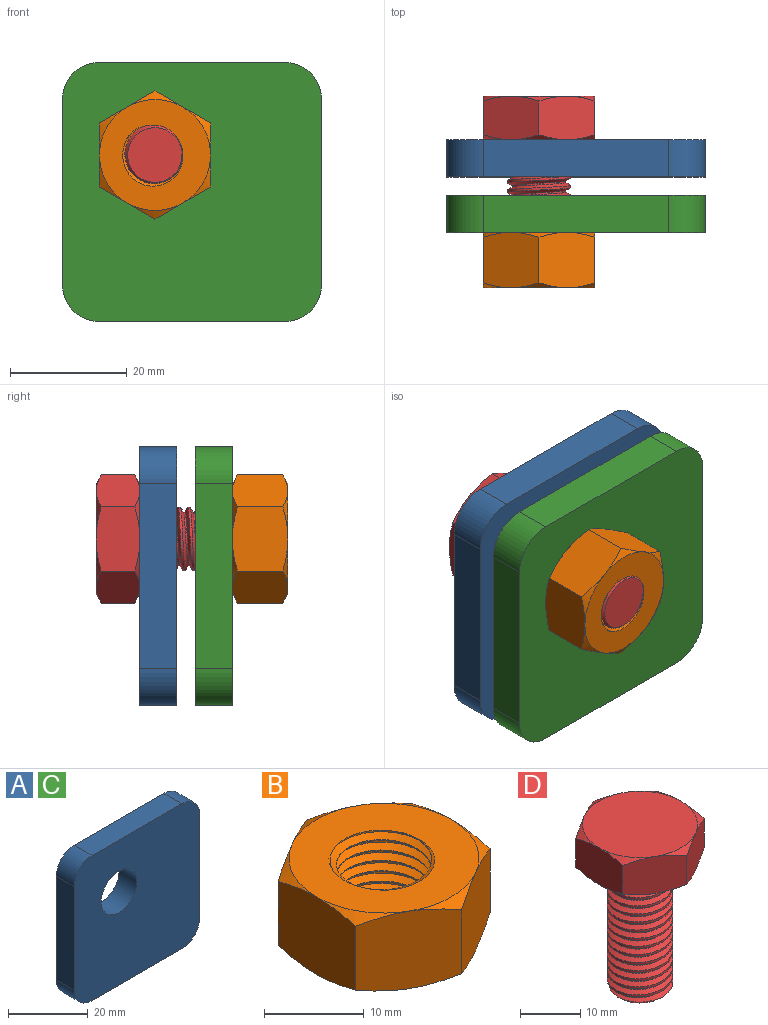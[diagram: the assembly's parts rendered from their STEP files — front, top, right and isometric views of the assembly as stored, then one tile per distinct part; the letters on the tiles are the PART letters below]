
ASSEMBLY  parts=4 mates=3
PART A: 11 faces, bbox 44.5x6.4x44.5 mm
  f0: plane 31.75x6.35mm, normal (0,0,-1), area 201.6mm2, adj f5,f6,f7,f10
  f1: plane 31.75x6.35mm, normal (1,0,0), area 201.6mm2, adj f5,f6,f7,f8
  f2: plane 31.75x6.35mm, normal (0,0,1), area 201.6mm2, adj f5,f6,f8,f9
  f3: cylinder r=6.35mm len=12.7mm, axis (0,1,0), area 253.4mm2, adj f5,f6
  f4: plane 31.75x6.35mm, normal (-1,0,0), area 201.6mm2, adj f5,f6,f9,f10
  f5: plane 44.45x44.45mm, normal (0,-1,0), area 1814.5mm2, adj f0,f1,f2,f3,f4,f7,f8,f9
  f6: plane 44.45x44.45mm, normal (0,1,0), area 1814.5mm2, adj f0,f1,f2,f3,f4,f7,f8,f9
  f7: cylinder r=6.35mm len=6.35mm, axis (0,1,0), area 63.3mm2, adj f0,f1,f5,f6
  f8: cylinder r=6.35mm len=6.35mm, axis (0,1,0), area 63.3mm2, adj f1,f2,f5,f6
  f9: cylinder r=6.35mm len=6.35mm, axis (0,1,0), area 63.3mm2, adj f2,f4,f5,f6
  f10: cylinder r=6.35mm len=6.35mm, axis (0,1,0), area 63.3mm2, adj f0,f4,f5,f6
PART B: 25 faces, bbox 22.9x22.9x11 mm
  f0: plane 19.49x19.49mm, normal (0,0,1), area 199.5mm2, adj f2,f5,f6,f8,f10,f12,f14,f22
  f1: plane 19.05x19.05mm, normal (0,0,-1), area 213.1mm2, adj f2,f3,f4,f7,f9,f11,f13
  f2: cylinder r=4.78mm len=9.57mm, axis (0,0,-1), area 65.3mm2, adj f0,f1,f21,f22,f23
  f3: cone r=15.51mm half-angle=60deg, axis (0,0,1), area 8.9mm2, adj f1,f15,f16
  f4: cone r=15.51mm half-angle=60deg, axis (0,0,1), area 8.9mm2, adj f1,f15,f20
  f5: cone r=15.51mm half-angle=60deg, axis (0,0,-1), area 8.9mm2, adj f0,f15,f16
  f6: cone r=15.51mm half-angle=60deg, axis (0,0,-1), area 8.9mm2, adj f0,f15,f20
  f7: cone r=15.51mm half-angle=60deg, axis (0,0,1), area 8.9mm2, adj f1,f16,f17
  f8: cone r=15.51mm half-angle=60deg, axis (0,0,-1), area 8.9mm2, adj f0,f16,f17
  f9: cone r=15.51mm half-angle=60deg, axis (0,0,1), area 8.9mm2, adj f1,f17,f18
  f10: cone r=15.51mm half-angle=60deg, axis (0,0,-1), area 8.9mm2, adj f0,f17,f18
  f11: cone r=15.51mm half-angle=60deg, axis (0,0,1), area 8.9mm2, adj f1,f18,f19
  f12: cone r=15.51mm half-angle=60deg, axis (0,0,-1), area 8.9mm2, adj f0,f18,f19
  f13: cone r=15.51mm half-angle=60deg, axis (0,0,1), area 8.9mm2, adj f1,f19,f20
  f14: cone r=15.51mm half-angle=60deg, axis (0,0,-1), area 8.9mm2, adj f0,f19,f20
  f15: plane 10.43x10.43mm, normal (-0.5,0.87,0), area 98.3mm2, adj f3,f4,f5,f6,f16,f20
  f16: plane 10.43x10.43mm, normal (0.5,0.87,0), area 98.3mm2, adj f3,f5,f7,f8,f15,f17
  f17: plane 11.91x10.44mm, normal (1,0,0), area 98.3mm2, adj f7,f8,f9,f10,f16,f18
  f18: plane 10.43x10.43mm, normal (0.5,-0.87,0), area 98.3mm2, adj f9,f10,f11,f12,f17,f19
  f19: plane 10.43x10.43mm, normal (-0.5,-0.87,0), area 98.3mm2, adj f11,f12,f13,f14,f18,f20
  f20: plane 11.91x10.44mm, normal (-1,0,0), area 98.3mm2, adj f4,f6,f13,f14,f15,f19
  f21: plane 1.15x0.76mm, normal (0,-1,0), area 0.5mm2, adj f2,f22,f23,f24
  f22: bspline ~12.79x11.08mm, area 191.6mm2, adj f0,f2,f21,f24
  f23: bspline ~12.79x11.08mm, area 205.7mm2, adj f0,f2,f21,f24
  f24: cylinder r=5.54mm len=11.08mm, axis (0,0,-1), area 90.5mm2, adj f0,f21,f22,f23
PART C: same geometry as A
PART D: 28 faces, bbox 22.9x22.9x34.3 mm
  f0: cylinder r=5.44mm len=24.65mm, axis (0,0,1), area 211.7mm2, adj f20,f22,f24,f25,f27
  f1: plane 9.39x9.39mm, normal (0,0,-1), area 69mm2, adj f22,f23,f25,f26
  f2: plane 11.91x8.41mm, normal (-1,0,0), area 76.1mm2, adj f3,f7,f8,f9,f10,f11
  f3: plane 10.43x8.41mm, normal (-0.5,0.87,0), area 76.1mm2, adj f2,f4,f8,f10,f12,f13
  f4: plane 10.43x8.41mm, normal (0.5,0.87,0), area 76.1mm2, adj f3,f5,f12,f13,f14,f15
  f5: plane 11.91x8.41mm, normal (1,0,0), area 76.1mm2, adj f4,f6,f14,f15,f16,f17
  f6: plane 10.43x8.41mm, normal (0.5,-0.87,0), area 76.1mm2, adj f5,f7,f16,f17,f18,f19
  f7: plane 10.43x8.41mm, normal (-0.5,-0.87,0), area 76.1mm2, adj f2,f6,f9,f11,f18,f19
  f8: cone r=13.05mm half-angle=60deg, axis (0,0,1), area 8.9mm2, adj f2,f3,f20
  f9: cone r=13.05mm half-angle=60deg, axis (0,0,1), area 8.9mm2, adj f2,f7,f20
  f10: cone r=13.05mm half-angle=60deg, axis (0,0,-1), area 8.9mm2, adj f2,f3,f21
  f11: cone r=13.05mm half-angle=60deg, axis (0,0,-1), area 8.9mm2, adj f2,f7,f21
  f12: cone r=13.05mm half-angle=60deg, axis (0,0,1), area 8.9mm2, adj f3,f4,f20
  f13: cone r=13.05mm half-angle=60deg, axis (0,0,-1), area 8.9mm2, adj f3,f4,f21
  f14: cone r=13.05mm half-angle=60deg, axis (0,0,1), area 8.9mm2, adj f4,f5,f20
  f15: cone r=13.05mm half-angle=60deg, axis (0,0,-1), area 8.9mm2, adj f4,f5,f21
  f16: cone r=13.05mm half-angle=60deg, axis (0,0,1), area 8.9mm2, adj f5,f6,f20
  f17: cone r=13.05mm half-angle=60deg, axis (0,0,-1), area 8.9mm2, adj f5,f6,f21
  f18: cone r=13.05mm half-angle=60deg, axis (0,0,1), area 8.9mm2, adj f6,f7,f20
  f19: cone r=13.05mm half-angle=60deg, axis (0,0,-1), area 8.9mm2, adj f6,f7,f21
  f20: plane 19.05x19.05mm, normal (0,0,-1), area 192.2mm2, adj f0,f8,f9,f12,f14,f16,f18
  f21: plane 19.05x19.05mm, normal (0,0,1), area 285mm2, adj f10,f11,f13,f15,f17,f19
  f22: cone r=4.69mm half-angle=45deg, axis (0,0,1), area 20.3mm2, adj f0,f1,f23,f25
  f23: plane 0.82x0.75mm, normal (0,1,0), area 0.1mm2, adj f1,f22,f26,f27
  f24: plane 1.23x0.82mm, normal (0,-1,0), area 0.6mm2, adj f0,f25,f26,f27
  f25: bspline ~25.13x12.56mm, area 439.1mm2, adj f0,f1,f22,f24,f26
  f26: cylinder r=4.61mm len=24.92mm, axis (0,0,1), area 121.6mm2, adj f1,f23,f24,f25,f27
  f27: bspline ~25.13x12.56mm, area 450mm2, adj f0,f23,f24,f26
PLACE A t=(10.06,-21.29,11.29)mm
PLACE B rot(axis=(1,0,0),90deg) t=(-18.52,-33.99,17.64)mm
PLACE C t=(10.06,-30.82,11.29)mm
PLACE D rot(axis=(-1,0,0),90deg) t=(-18.52,-18.12,17.64)mm
MATE fastened D.f8 <-> A.f3  axis (0,-1,0) through (-18.52,-18.12,17.64)mm
MATE fastened C.f3 <-> A.f3  axis (0,1,0) through (-18.52,-27.64,17.64)mm
MATE fastened C.f3 <-> B.f3  axis (0,-1,0) through (-18.52,-33.99,17.64)mm
